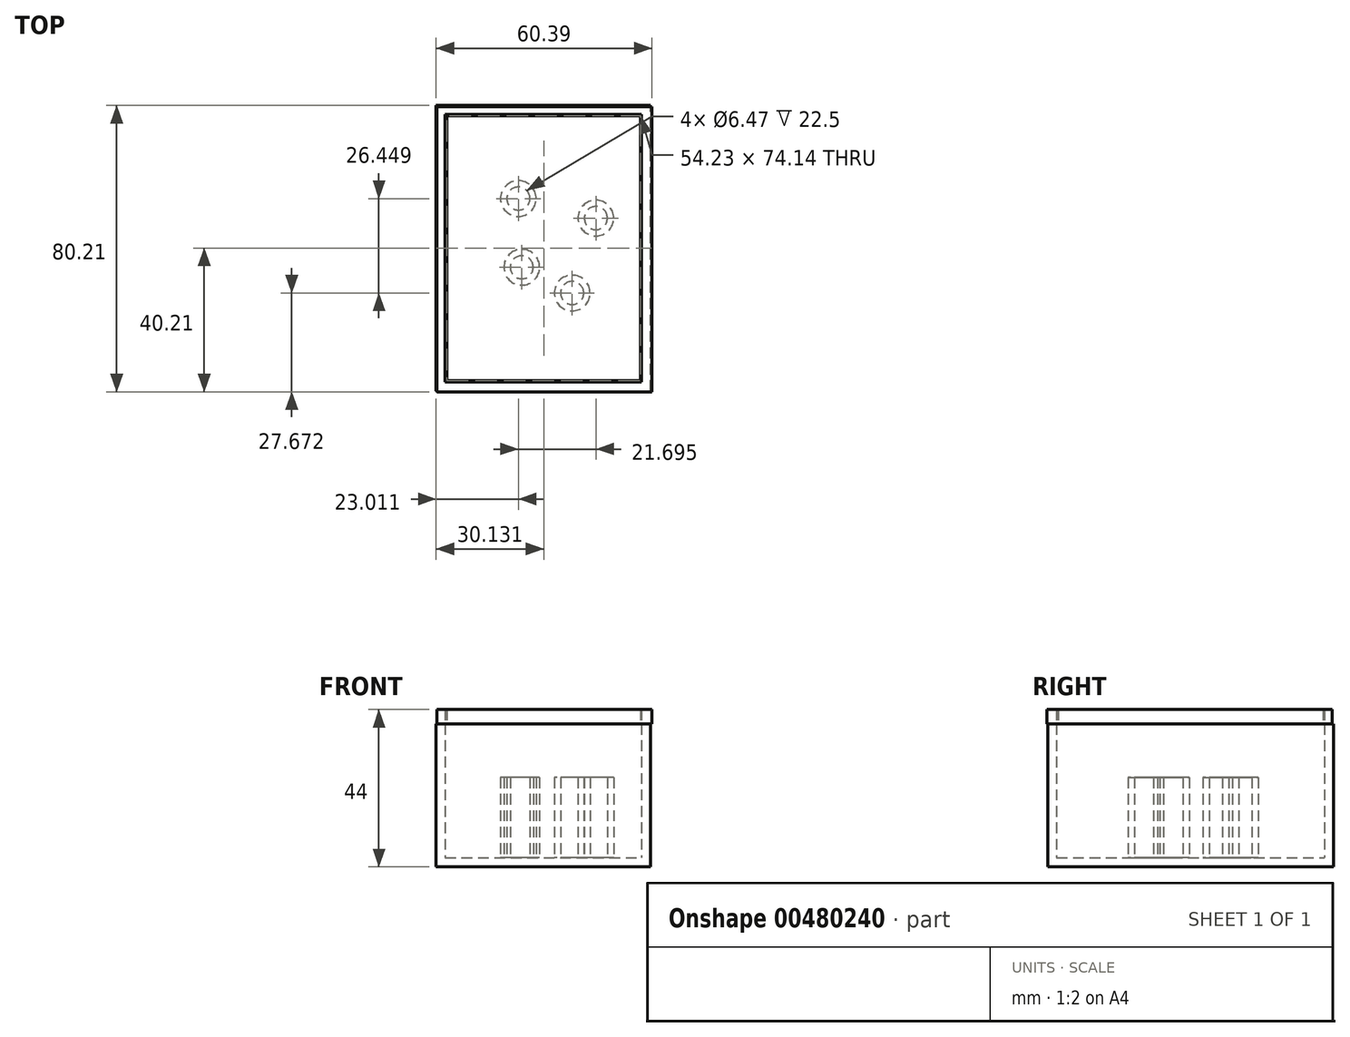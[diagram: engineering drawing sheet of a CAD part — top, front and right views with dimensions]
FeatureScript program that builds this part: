
annotation { "Feature Type Name" : "Feature", "Feature Type Description" : "" }
export const myFeature = defineFeature(function(context is Context, id is Id, definition is map)
    precondition{}
    {
        {
            var Q0;
            Q0=qCreatedBy(makeId("Top.planeOp"),FACE);
            var sketch = newSketch(context, id + "F0", { "sketchPlane" : qUnion([Q0])});
            skLineSegment(sketch, "E0.bottom", {"start": v(-30, -40) * mm, "end": v(30, -40) * mm});
            skLineSegment(sketch, "E0.top", {"start": v(-30, 40) * mm, "end": v(30, 40) * mm});
            skLineSegment(sketch, "E0.left", {"start": v(-30, -40) * mm, "end": v(-30, 40) * mm});
            skLineSegment(sketch, "E0.right", {"start": v(30, -40) * mm, "end": v(30, 40) * mm});
            skPoint(sketch, "E0.middle", {"position": v(0, 0) * mm});
            skSolve(sketch);
        }
        {
            var Q0;
            Q0=makeQuery(id+"F0.imprint","IMPRINT",FACE,{"disambiguationData":[TD([[makeQuery(id+"F0.imprint","IMPRINT",EDGE,{"derivedFrom":sQuery(id+"F0.wireOp",EDGE,"E0.bottom")}),1.0]])]});
            extrude(context, id + "F1", {"entities" : qUnion([Q0]), "depth" : 40 * mm});
        }
        {
            var Q0;
            Q0=makeQuery(id+"F1.opExtrude","CAP_FACE",FACE,{"disambiguationData":[OSD([sQuery(id+"F0.wireOp",EDGE,"E0.bottom"),sQuery(id+"F0.wireOp",EDGE,"E0.top"),sQuery(id+"F0.wireOp",EDGE,"E0.left"),sQuery(id+"F0.wireOp",EDGE,"E0.right")])],"isStart":false});
            shell(context, id + "F2", {"entities" : qUnion([Q0]), "thickness" : 2.5 * mm});
        }
        {
            var Q0;
            Q0=makeQuery(id+"F1.opExtrude","CAP_FACE",FACE,{"disambiguationData":[OSD([sQuery(id+"F0.wireOp",EDGE,"E0.bottom"),sQuery(id+"F0.wireOp",EDGE,"E0.top"),sQuery(id+"F0.wireOp",EDGE,"E0.left"),sQuery(id+"F0.wireOp",EDGE,"E0.right")])],"isStart":false});
            var sketch = newSketch(context, id + "F3", { "sketchPlane" : qUnion([Q0])});
            skSolve(sketch);
        }
        {
            var Q0;
            {var subQ0=sQuery(id+"F0.wireOp",EDGE,"E0.bottom");Q0=makeQuery(id+"F3.imprint","IMPRINT",FACE,{"disambiguationData":[TD([[makeQuery(id+"F3.imprint","IMPRINT",EDGE,{"derivedFrom":makeQuery(id+"F2.opShell","OFFSET_EDGE",EDGE,{"disambiguationData":[OSD([subQ0]),TDD([makeQuery(id+"F1.opExtrude","CAP_EDGE",EDGE,{"disambiguationData":[OSD([subQ0])],"isStart":false})])]})}),1.0]])]});}
            var sketch = newSketch(context, id + "F4", { "sketchPlane" : qUnion([Q0])});
            skLineSegment(sketch, "E1.bottom", {"start": v(-29.86, 39.69) * mm, "end": v(30.39, 39.69) * mm});
            skLineSegment(sketch, "E1.top", {"start": v(-29.86, -40.21) * mm, "end": v(30.39, -40.21) * mm});
            skLineSegment(sketch, "E1.left", {"start": v(-29.86, 39.69) * mm, "end": v(-29.86, -40.21) * mm});
            skLineSegment(sketch, "E1.right", {"start": v(30.39, 39.69) * mm, "end": v(30.39, -40.21) * mm});
            skLineSegment(sketch, "E2.bottom", {"start": v(-26.98, 37.07) * mm, "end": v(27.25, 37.07) * mm});
            skLineSegment(sketch, "E2.top", {"start": v(-26.98, -37.07) * mm, "end": v(27.25, -37.07) * mm});
            skLineSegment(sketch, "E2.left", {"start": v(-26.98, 37.07) * mm, "end": v(-26.98, -37.07) * mm});
            skLineSegment(sketch, "E2.right", {"start": v(27.25, 37.07) * mm, "end": v(27.25, -37.07) * mm});
            skSolve(sketch);
        }
        {
            var Q0;
            Q0 = qSketchRegion(id + "F4", true);
            var Q1;
            {var subQ0=sQuery(id+"F0.wireOp",EDGE,"E0.bottom");Q1=makeQuery(id+"F3.imprint","IMPRINT",FACE,{"disambiguationData":[TD([[makeQuery(id+"F3.imprint","IMPRINT",EDGE,{"derivedFrom":makeQuery(id+"F2.opShell","OFFSET_EDGE",EDGE,{"disambiguationData":[OSD([subQ0]),TDD([makeQuery(id+"F1.opExtrude","CAP_EDGE",EDGE,{"disambiguationData":[OSD([subQ0])],"isStart":false})])]})}),1.0]])]});}
            extrude(context, id + "F5", {"entities" : qUnion([Q0, Q1]), "depth" : 4 * mm});
        }
        {
            var Q0;
            Q0=makeQuery(id+"F0.imprint","IMPRINT",FACE,{"disambiguationData":[TD([[makeQuery(id+"F0.imprint","IMPRINT",EDGE,{"derivedFrom":sQuery(id+"F0.wireOp",EDGE,"E0.bottom")}),1.0]])]});
            var sketch = newSketch(context, id + "F6", { "sketchPlane" : qUnion([Q0])});
            skCircle(sketch, "E3", {"center": v(-6.99, 13.91) * mm, "radius": 3.24 * mm});
            skCircle(sketch, "E4", {"center": v(14.7, 8.44) * mm, "radius": 3.24 * mm});
            skCircle(sketch, "E5", {"center": v(-6.05, -5.33) * mm, "radius": 3.24 * mm});
            skCircle(sketch, "E6", {"center": v(8.07, -12.54) * mm, "radius": 3.24 * mm});
            skCircle(sketch, "E7", {"center": v(-6.05, -5.33) * mm, "radius": 5 * mm});
            skCircle(sketch, "E8", {"center": v(-6.99, 13.91) * mm, "radius": 5 * mm});
            skCircle(sketch, "E9", {"center": v(14.7, 8.44) * mm, "radius": 5 * mm});
            skCircle(sketch, "E10", {"center": v(8.07, -12.54) * mm, "radius": 5 * mm});
            skSolve(sketch);
        }
        {
            var Q0;
            Q0 = qSketchRegion(id + "F6", true);
            extrude(context, id + "F7", {"entities" : qUnion([Q0]), "operationType" : NewBodyOperationType.ADD, "depth" : 25 * mm});
        }
    });
